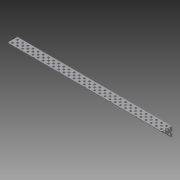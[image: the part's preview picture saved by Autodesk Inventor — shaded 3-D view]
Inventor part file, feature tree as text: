
AUTODESK INVENTOR PART (.ipt)
format: ipt  version: 2014 SP1 (Build 180222100, 222)  size: 2,078,720 bytes
history: native  units: in
note: dims shown in document units (in); Inventor stores cm internally (conversion verified against a paired STEP export)
features: other x1, imported_body x1, extrude x1, sketch x1, projected_geometry x1
ambient origin geometry x8: Origin, YZ Plane, XZ Plane, XY Plane, X Axis, Y Axis, Z Axis, Center Point
bodies: Body1 (feature_tree)
feature tree (5):
  parser-record x1  (decoder bookkeeping rows leaked as tree rows — omitted from the tree; the rows remain in map.json)
  imported_body  "Base1"
  extrude  "Extrusion1"  [1 undecoded]
  sketch  "Sketch1"  dims[d0=1.0in d1=0.0in]
  projected_geometry  "Projected Loop1"
note: 1 required parameter value undecoded (feature->parameter linkage not recoverable at this tier; creation-order binding heuristic only, values carry confidence <= 0.55)
